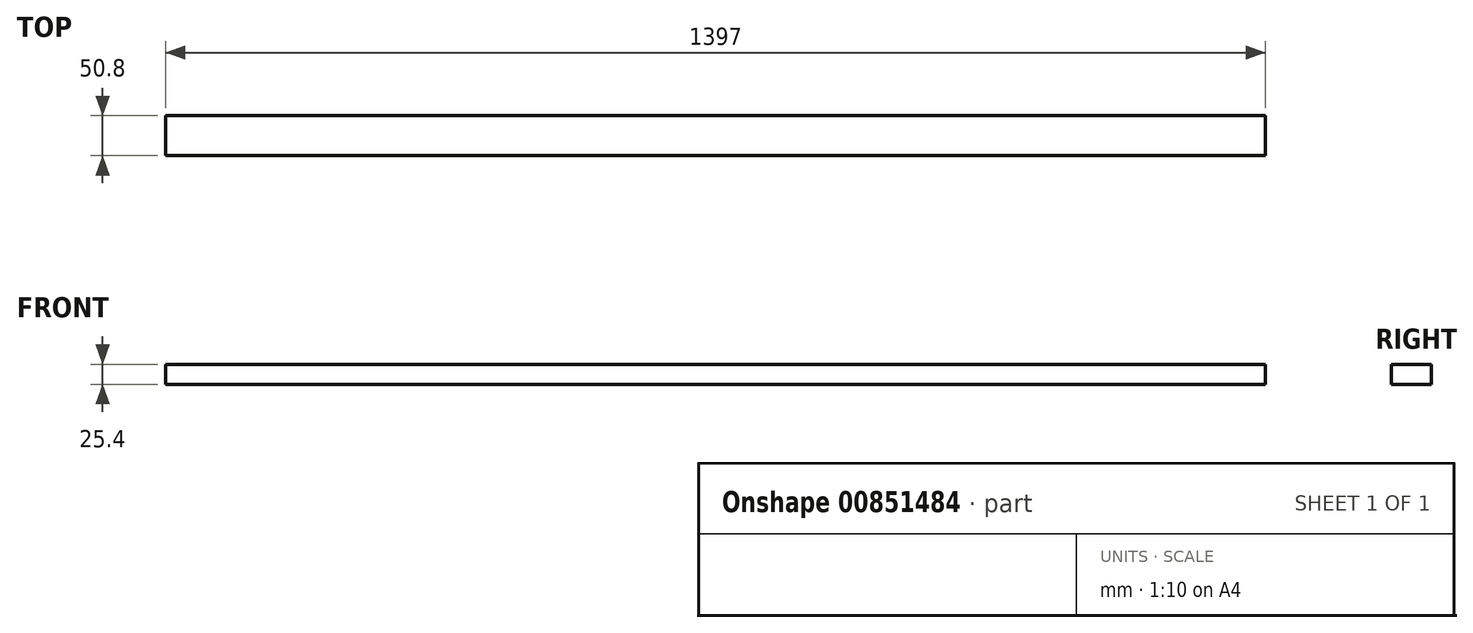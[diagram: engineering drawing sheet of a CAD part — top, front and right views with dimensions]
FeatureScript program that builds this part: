
annotation { "Feature Type Name" : "Feature", "Feature Type Description" : "" }
export const myFeature = defineFeature(function(context is Context, id is Id, definition is map)
    precondition{}
    {
        {
            var Q0;
            Q0=qCreatedBy(makeId("Front.planeOp"),FACE);
            var sketch = newSketch(context, id + "F0", { "sketchPlane" : qUnion([Q0])});
            skLineSegment(sketch, "E0.bottom", {"start": v(-691.75, -217.74) * mm, "end": v(705.25, -217.74) * mm});
            skLineSegment(sketch, "E0.top", {"start": v(-691.75, -243.14) * mm, "end": v(705.25, -243.14) * mm});
            skLineSegment(sketch, "E0.left", {"start": v(-691.75, -217.74) * mm, "end": v(-691.75, -243.14) * mm});
            skLineSegment(sketch, "E0.right", {"start": v(705.25, -217.74) * mm, "end": v(705.25, -243.14) * mm});
            skSolve(sketch);
        }
        {
            var Q0;
            Q0 = qSketchRegion(id + "F0", true);
            extrude(context, id + "F1", {"entities" : qUnion([Q0]), "depth" : 50.8 * mm, "offsetDistance" : 25.4 * mm});
        }
    });
